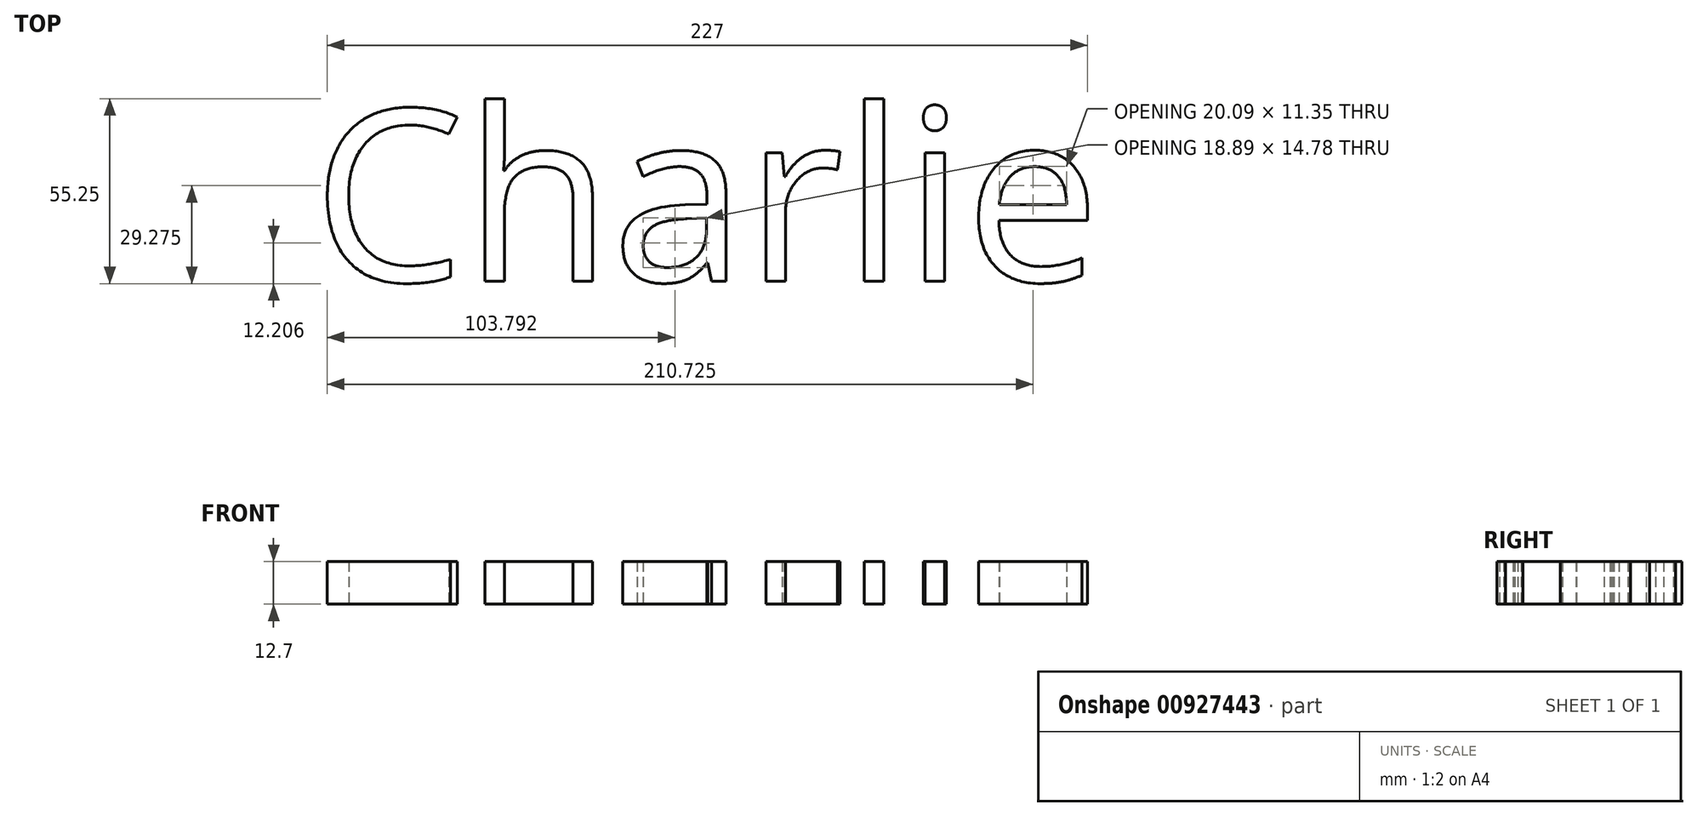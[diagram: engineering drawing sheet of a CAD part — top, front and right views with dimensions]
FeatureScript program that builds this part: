
annotation { "Feature Type Name" : "Feature", "Feature Type Description" : "" }
export const myFeature = defineFeature(function(context is Context, id is Id, definition is map)
    precondition{}
    {
        {
            var Q0;
            Q0=qCreatedBy(makeId("Top.planeOp"),FACE);
            var sketch = newSketch(context, id + "F0", { "sketchPlane" : qUnion([Q0])});
            skText(sketch, "E0", { "text": "Charlie", "fontName": "OpenSans-Regular.ttf"});
            const initialGuessF0  = {"E0": [-0.11644, -0.02265, 1, 0, 0.05168]};
            skSetInitialGuess(sketch, initialGuessF0);
            skSolve(sketch);
        }
        {
            var Q0;
            Q0 = qSketchRegion(id + "F0", true);
            extrude(context, id + "F1", {"entities" : qUnion([Q0]), "endBound" : BoundingType.SYMMETRIC, "depth" : 12.7 * mm, "offsetDistance" : 25.4 * mm});
        }
    });
